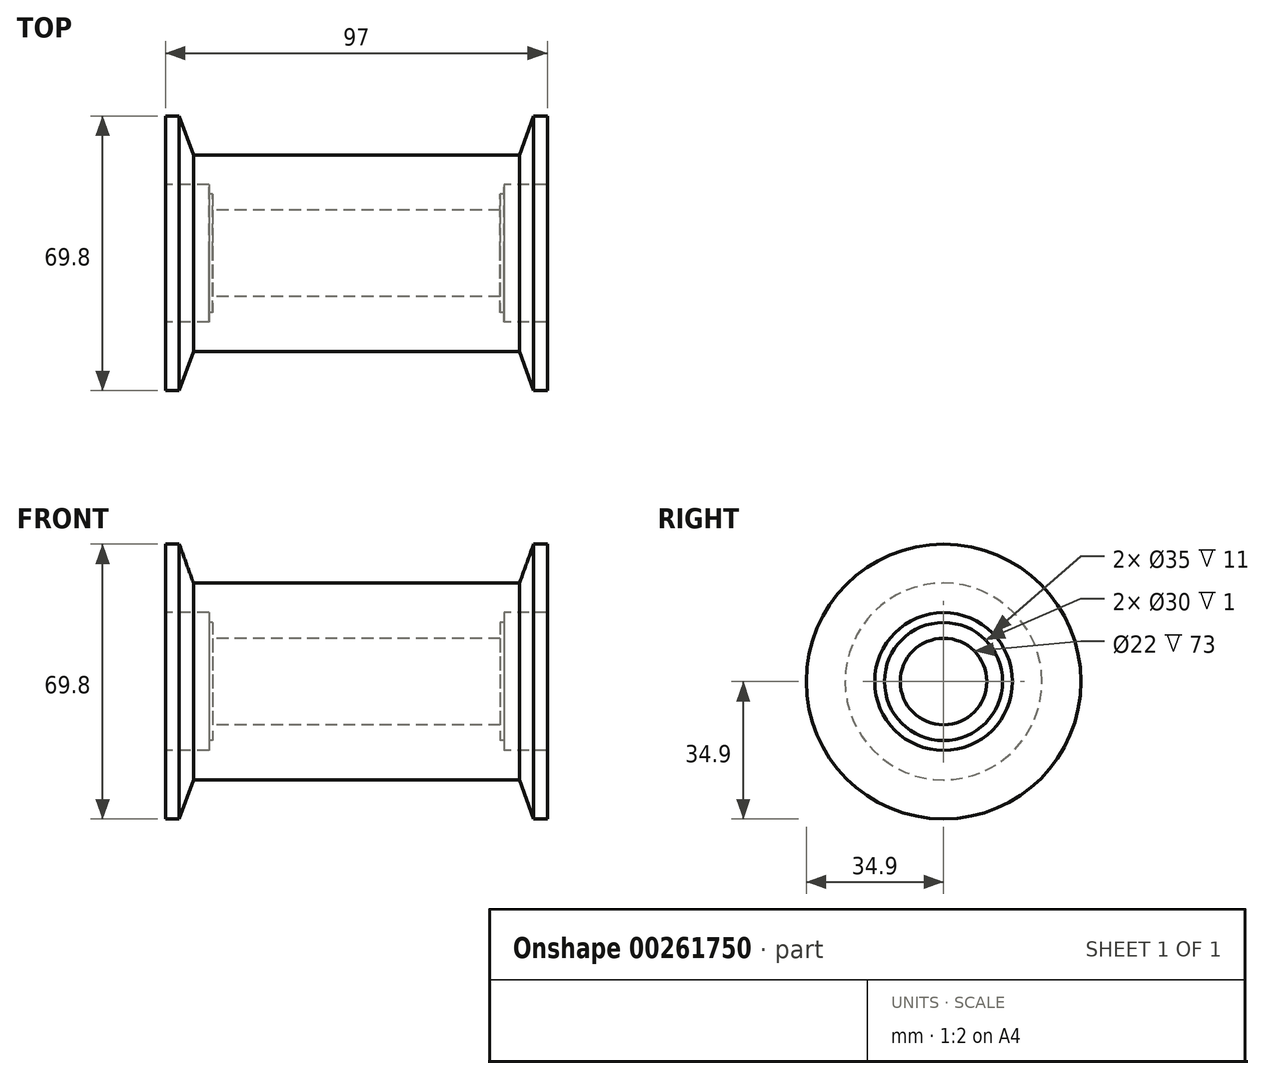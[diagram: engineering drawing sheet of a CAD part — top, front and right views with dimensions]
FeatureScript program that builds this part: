
annotation { "Feature Type Name" : "Feature", "Feature Type Description" : "" }
export const myFeature = defineFeature(function(context is Context, id is Id, definition is map)
    precondition{}
    {
        {
            var Q0;
            Q0=qCreatedBy(makeId("Front.planeOp"),FACE);
            var sketch = newSketch(context, id + "F0", { "sketchPlane" : qUnion([Q0])});
            skLineSegment(sketch, "E0", {"start": v(0, 25) * mm, "end": v(41.4, 25) * mm});
            skLineSegment(sketch, "E1", {"start": v(41.4, 25) * mm, "end": v(45, 34.9) * mm});
            skLineSegment(sketch, "E2", {"start": v(45, 34.9) * mm, "end": v(48.5, 34.9) * mm});
            skLineSegment(sketch, "E3", {"start": v(48.5, 34.9) * mm, "end": v(48.5, 17.5) * mm});
            skLineSegment(sketch, "E4", {"start": v(48.5, 17.5) * mm, "end": v(37.5, 17.5) * mm});
            skLineSegment(sketch, "E5", {"start": v(37.5, 17.5) * mm, "end": v(37.5, 15) * mm});
            skLineSegment(sketch, "E6", {"start": v(37.5, 15) * mm, "end": v(36.5, 15) * mm});
            skLineSegment(sketch, "E7", {"start": v(36.5, 15) * mm, "end": v(36.5, 11) * mm});
            skLineSegment(sketch, "E8", {"start": v(36.5, 11) * mm, "end": v(0, 11) * mm});
            skLineSegment(sketch, "E9.MirrorCS", {"start": v(0, 25) * mm, "end": v(-41.4, 25) * mm});
            skLineSegment(sketch, "E10.MirrorCS", {"start": v(-41.4, 25) * mm, "end": v(-45, 34.9) * mm});
            skLineSegment(sketch, "E11.MirrorCS", {"start": v(-45, 34.9) * mm, "end": v(-48.5, 34.9) * mm});
            skLineSegment(sketch, "E12.MirrorCS", {"start": v(-48.5, 34.9) * mm, "end": v(-48.5, 17.5) * mm});
            skLineSegment(sketch, "E13.MirrorCS", {"start": v(-48.5, 17.5) * mm, "end": v(-37.5, 17.5) * mm});
            skLineSegment(sketch, "E14.MirrorCS", {"start": v(-37.5, 17.5) * mm, "end": v(-37.5, 15) * mm});
            skLineSegment(sketch, "E15.MirrorCS", {"start": v(-37.5, 15) * mm, "end": v(-36.5, 15) * mm});
            skLineSegment(sketch, "E16.MirrorCS", {"start": v(-36.5, 15) * mm, "end": v(-36.5, 11) * mm});
            skLineSegment(sketch, "E17.MirrorCS", {"start": v(-36.5, 11) * mm, "end": v(0, 11) * mm});
            skLineSegment(sketch, "E18", {"start": v(-64.48, 0) * mm, "end": v(70.9, 0) * mm, "construction": true});
            skSolve(sketch);
        }
        {
            var Q0;
            Q0=makeQuery(id+"F0.imprint","IMPRINT",FACE,{"disambiguationData":[TD([[makeQuery(id+"F0.imprint","IMPRINT",EDGE,{"derivedFrom":sQuery(id+"F0.wireOp",EDGE,"E0")}),-1.0]])]});
            var Q1;
            Q1=sQuery(id+"F0.wireOp",EDGE,"E18");
            revolve(context, id + "F1", {"entities" : qUnion([Q0]), "axis" : qUnion([Q1]), "revolveType" : RevolveType.FULL});
        }
    });
